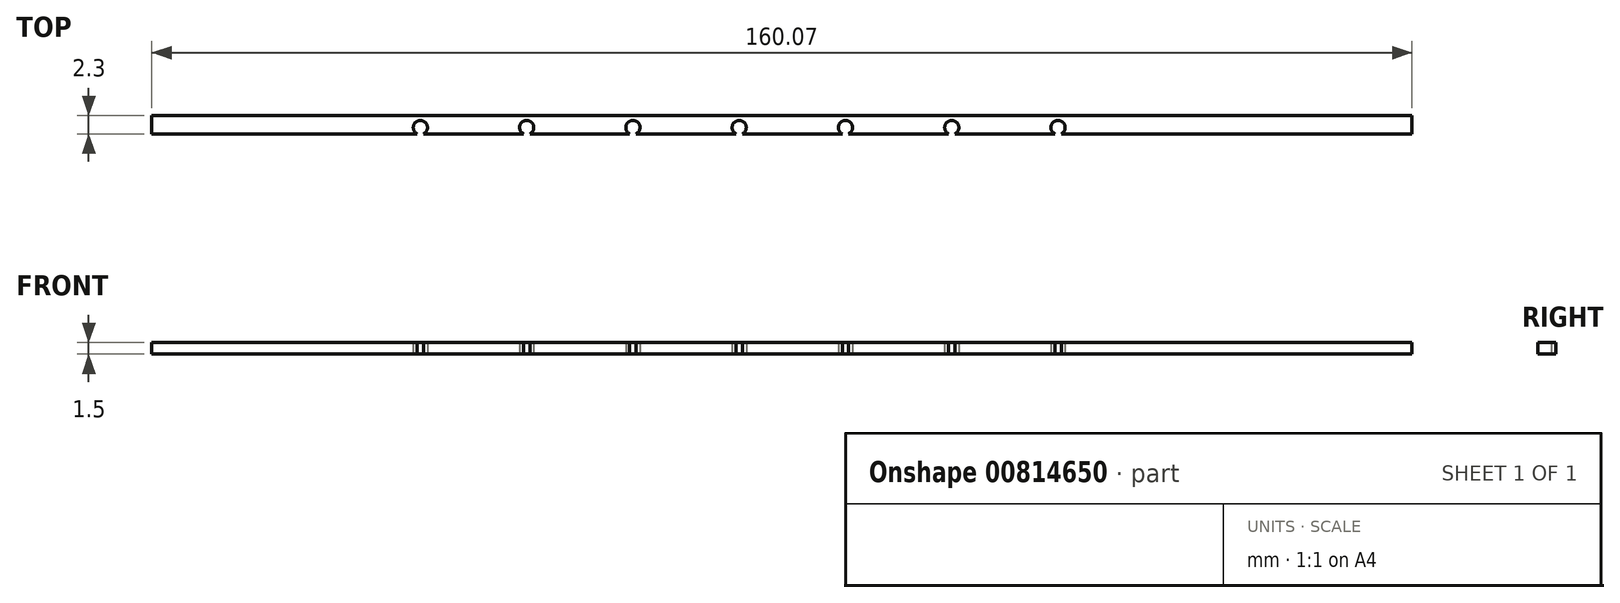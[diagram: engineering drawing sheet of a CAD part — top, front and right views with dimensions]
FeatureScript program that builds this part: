
annotation { "Feature Type Name" : "Feature", "Feature Type Description" : "" }
export const myFeature = defineFeature(function(context is Context, id is Id, definition is map)
    precondition{}
    {
        {
            var Q0;
            Q0=qCreatedBy(makeId("Front.planeOp"),FACE);
            var sketch = newSketch(context, id + "F0", { "sketchPlane" : qUnion([Q0])});
            skLineSegment(sketch, "E0.bottom", {"start": v(-70.48, -6.66) * mm, "end": v(89.6, -6.66) * mm});
            skLineSegment(sketch, "E0.top", {"start": v(-70.48, -8.16) * mm, "end": v(89.6, -8.16) * mm});
            skLineSegment(sketch, "E0.left", {"start": v(-70.48, -6.66) * mm, "end": v(-70.48, -8.16) * mm});
            skLineSegment(sketch, "E0.right", {"start": v(89.6, -6.66) * mm, "end": v(89.6, -8.16) * mm});
            skSolve(sketch);
        }
        {
            var Q0;
            Q0=qSketchRegion(id+"F0",true);
            extrude(context, id + "F1", {"entities" : qUnion([Q0]), "depth" : 2.3 * mm, "offsetDistance" : 25.4 * mm});
        }
        {
            var Q0;
            Q0=makeQuery(id+"F1.opExtrude","SWEPT_FACE",FACE,{"disambiguationData":[OSD([sQuery(id+"F0.wireOp",EDGE,"E0.top")])]});
            var sketch = newSketch(context, id + "F2", { "sketchPlane" : qUnion([Q0])});
            skPoint(sketch, "E1", {"position": v(-36.36, 1.5) * mm});
            skPoint(sketch, "E2", {"position": v(-22.86, 1.5) * mm});
            skPoint(sketch, "E3.2.0.0", {"position": v(-9.36, 1.5) * mm});
            skPoint(sketch, "E3.3.0.0", {"position": v(4.14, 1.5) * mm});
            skPoint(sketch, "E3.4.0.0", {"position": v(17.64, 1.5) * mm});
            skPoint(sketch, "E3.5.0.0", {"position": v(31.14, 1.5) * mm});
            skPoint(sketch, "E3.6.0.0", {"position": v(44.64, 1.5) * mm});
            skLineSegment(sketch, "E3.direction1", {"start": v(-38.65, 1.5) * mm, "end": v(50.18, 1.5) * mm, "construction": true});
            skSolve(sketch);
        }
        {
            var Q0;
            Q0=sQuery(id+"F2.wireOp",VERTEX,"E1");
            var Q1;
            Q1=sQuery(id+"F2.wireOp",VERTEX,"E2");
            var Q2;
            Q2=sQuery(id+"F2.wireOp",VERTEX,"E3.2.0.0");
            var Q3;
            Q3=sQuery(id+"F2.wireOp",VERTEX,"E3.3.0.0");
            var Q4;
            Q4=sQuery(id+"F2.wireOp",VERTEX,"E3.4.0.0");
            var Q5;
            Q5=sQuery(id+"F2.wireOp",VERTEX,"E3.5.0.0");
            var Q6;
            Q6=sQuery(id+"F2.wireOp",VERTEX,"E3.6.0.0");
            var Q7;
            Q7=makeQuery(id+"F1.opExtrude","SWEPT_BODY",BODY,{"disambiguationData":[OSD([sQuery(id+"F0.wireOp",EDGE,"E0.bottom"),sQuery(id+"F0.wireOp",EDGE,"E0.top"),sQuery(id+"F0.wireOp",EDGE,"E0.left"),sQuery(id+"F0.wireOp",EDGE,"E0.right")])]});
            hole(context, id + "F3", {"style" : HoleStyle.SIMPLE, "endStyle" : HoleEndStyle.BLIND, "holeDiameter" : 1.8 * mm, "majorDiameter" : 6.35 * mm, "holeDepth" : 1.6 * mm, "isTappedThrough" : true, "tappedDepth" : 12.7 * mm, "tapClearance" : 3, "locations" : qUnion([Q0, Q1, Q2, Q3, Q4, Q5, Q6]), "scope" : qUnion([Q7])});
        }
    });
